# Revit family: IRIS-L-A 11000-xx-T
name_source: partatom
category: Leuchten
units: mm (PartAtom-declared; Revit-internal decimal feet)

## family parameters
Basisbauteil = Fläche
Beim Laden mit Abzugskörper schneiden = Nein
Bemaßung runder Anschluss = Durchmesser verwenden
Gemeinsam genutzt = Nein
Lichtquelle = Ja
OmniClass-Nummer = 23.80.70.11
OmniClass-Titel = Luminaries for Internal Lighting
Raumberechnungspunkt = Nein
Teiletyp = Normal

## types (5) — shared parameters
Baugruppenkennzeichen = D5020200
Datei für fotometrisches Netz = IRIS-L-A 10000-840-DA.IES
Emissionsform beim Rendern sichtbar = Nein
Farbfilter = 16777215
Farbtemperaturverschiebung bei Dämpfen der Lampe = <Keine Auswahl>
Hersteller = RIDI Leuchten GmbH
Lampe = LED
Neigungswinkel = 90.00°
Scheinlast = 78 VA
URL = www.ridi.de
Von Kreisdurchmesser aussenden = 606 mm  [stored 1.98819 ft]
brand = RIDI
conformity mark = CE
electrical safety class = 1
height = 60 mm  [stored 0.19685 ft]
ingress protection (IP) code = IP20
length = 606 mm  [stored 1.98819 ft]
nominal frequency = 50-60Hz
nominal voltage = 230
rated input power = 78
voltage type (AC, DC, UC) = AC
weight = 6,4 kg
width = 606 mm  [stored 1.98819 ft]
zero-valued in all types: Vorgabe-Ansicht

## per-type parameters (varying)
| type | Modell |
| IRIS-L-A 11000-830-ND-T | SPI0000115AY |
| IRIS-L-A 11000-840-ND-T | SPI0000116AY |
| IRIS-L-A 11000-830-DA-T | SPI0000117AY |
| IRIS-L-A 11000-840-DA-T | SPI0000118AY |
| IRIS-L-A 11000-8TW-DA-T | SPI0000119AY |

note: column(s) folded — value = type name in every type: product name

note: [stored X ft] marks values corroborated as IEEE doubles in the binary element streams (Revit-internal decimal feet)
